# Revit family: CADS_Vent-Axia_Lo-CarbonSentinelKineticPlusE
name_source: partatom
category: Mechanical Equipment
revit_build: Autodesk Revit 2015 (Build: 20140223_1515(x64)
units: mm (PartAtom-declared; Revit-internal decimal feet)

## types (1)
- Plus E
    Apparent Load = 690 VA
    AssetType = Fixed
    Category = Pr_60_60_36:Heat recovery distribution equipment
    Color = White
    Description = Lo-Carbon Sentinel Kinetic Plus B Right
    DurationUnit = year
    ExpectedLife = 20
    Features = Humidistat
    IfcExportAs = IfcAirToAirHeatRecoveryType
    IfcExportType = USERDEFINED
    LeftHand = No
    Manufacturer = Vent-Axia Limited
    Material = ABS Plastic
    Model = Kinetic Plus E
    ModelNumber = 449059
    ModelReference = Kinetic Plus E
    Name = MVHR Unit
    NominalHeight = 635 mm  [stored 2.08333 ft]
    NominalLength = 785 mm
    NominalWidth = 550 mm
    NumberOfPoles = 1
    RatedCurrent = 3 A
    RatedVoltage = 230 V
    RightHand = Yes
    Shape = Rectangular
    Size = 550mm x 785mm x 635mm 
285mm x 550mm x 550mm
    SpigotConnLength = 250 mm  [stored 0.82021 ft]
    SpigotConnWidth = 210 mm  [stored 0.688976 ft]
    SpigotCrsLength = 520 mm  [stored 1.70604 ft]
    SpigotCrsWidth = 275 mm
    SpigotHeight = 87 mm  [stored 0.285433 ft]
    SpigotOffset = 133 mm
    Version = 1.0
    WarrantyDurationLabor = 2
    WarrantyDurationMotors = 5
    WarrantyDurationParts = 2
    WarrantyDurationUnit = year

note: [stored X ft] marks values corroborated as IEEE doubles in the binary element streams (Revit-internal decimal feet)

## geometry (parser evidence)
native form markers: Sweep x19
no freeform markers — native parametric forms only
